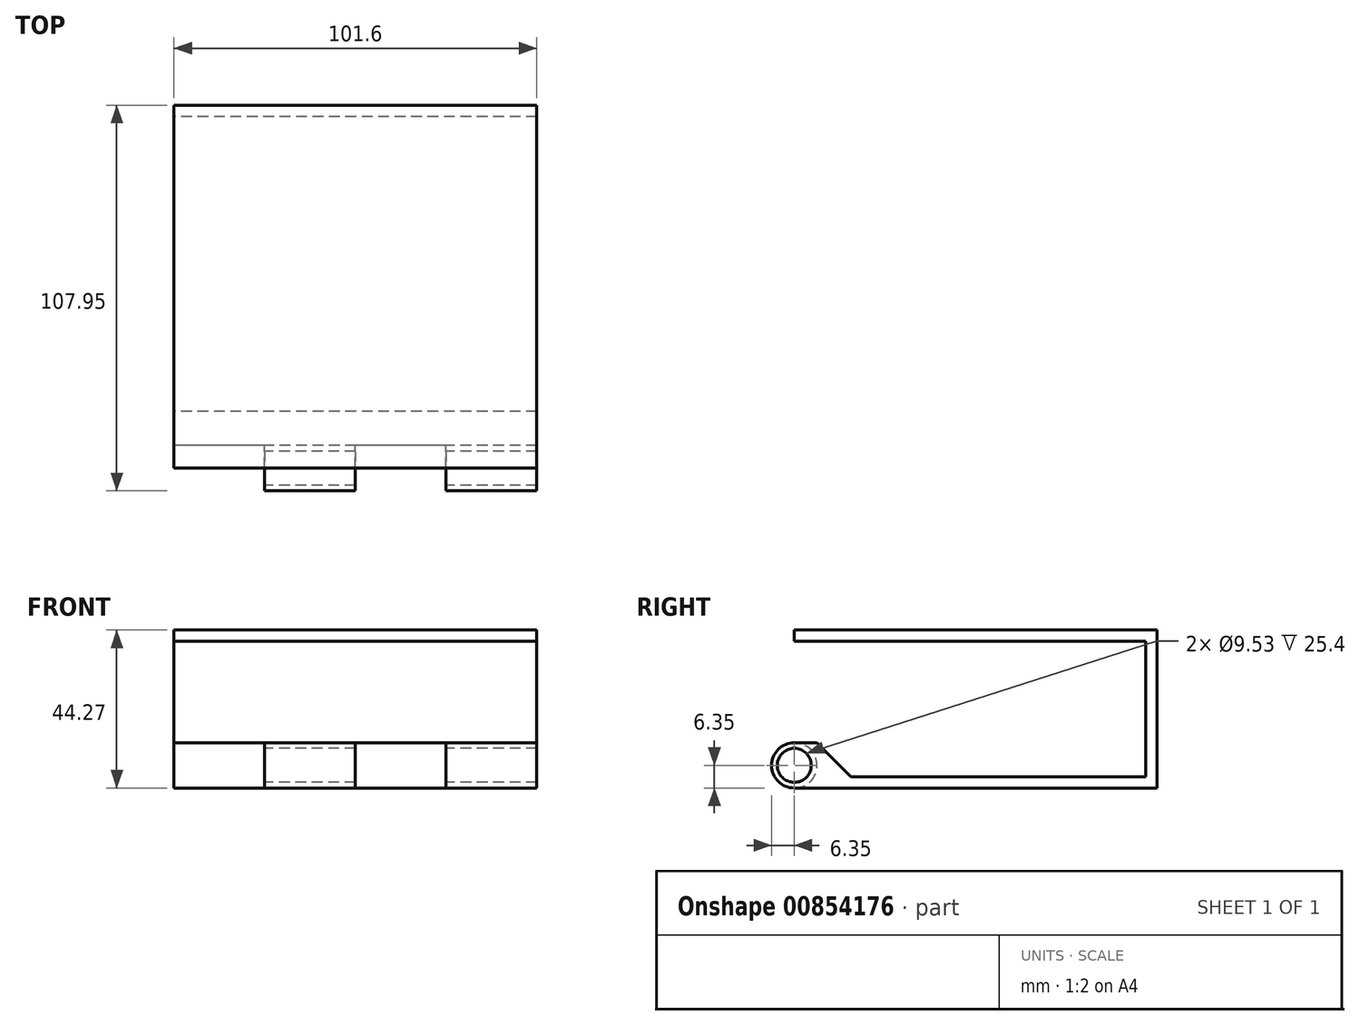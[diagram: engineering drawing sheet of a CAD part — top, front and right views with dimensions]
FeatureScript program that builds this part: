
annotation { "Feature Type Name" : "Feature", "Feature Type Description" : "" }
export const myFeature = defineFeature(function(context is Context, id is Id, definition is map)
    precondition{}
    {
        {
            var Q0;
            Q0=qCreatedBy(makeId("Right.planeOp"),FACE);
            var sketch = newSketch(context, id + "F0", { "sketchPlane" : qUnion([Q0])});
            skLineSegment(sketch, "E0.bottom", {"start": v(-44.45, 6.35) * mm, "end": v(-50.8, 6.35) * mm});
            skLineSegment(sketch, "E0.top", {"start": v(50.8, -6.35) * mm, "end": v(-50.8, -6.35) * mm});
            skLineSegment(sketch, "E0.left", {"start": v(50.8, 6.35) * mm, "end": v(50.8, -6.35) * mm});
            skLineSegment(sketch, "E0.right", {"start": v(-50.8, 6.35) * mm, "end": v(-50.8, -6.35) * mm});
            skPoint(sketch, "E0.middle", {"position": v(0, 0) * mm});
            skCircle(sketch, "E1", {"center": v(-50.8, 0) * mm, "radius": 6.35 * mm});
            skLineSegment(sketch, "E2", {"start": v(50.8, 6.35) * mm, "end": v(50.8, 37.92) * mm});
            skLineSegment(sketch, "E3", {"start": v(50.8, 37.92) * mm, "end": v(47.63, 37.92) * mm});
            skLineSegment(sketch, "E4", {"start": v(47.63, 34.74) * mm, "end": v(47.63, 6.35) * mm});
            skLineSegment(sketch, "E5.bottom", {"start": v(50.8, 37.92) * mm, "end": v(-50.8, 37.92) * mm});
            skLineSegment(sketch, "E5.top", {"start": v(47.62, 34.74) * mm, "end": v(-50.8, 34.74) * mm});
            skLineSegment(sketch, "E5.left", {"start": v(50.8, 34.74) * mm, "end": v(50.8, 37.92) * mm});
            skLineSegment(sketch, "E5.right", {"start": v(-50.8, 34.74) * mm, "end": v(-50.8, 37.92) * mm});
            skLineSegment(sketch, "E6", {"start": v(-44.45, 0) * mm, "end": v(-44.45, 6.35) * mm});
            skLineSegment(sketch, "E7", {"start": v(-44.45, 6.35) * mm, "end": v(-44.45, -6.35) * mm});
            skLineSegment(sketch, "E8", {"start": v(-44.45, 6.35) * mm, "end": v(-34.92, -3.18) * mm});
            skLineSegment(sketch, "E9", {"start": v(-34.92, -3.18) * mm, "end": v(47.63, -3.17) * mm});
            skLineSegment(sketch, "E10", {"start": v(47.62, -3.17) * mm, "end": v(47.62, 6.35) * mm});
            skCircle(sketch, "E11", {"center": v(-50.8, 0) * mm, "radius": 4.76 * mm});
            skSolve(sketch);
        }
        {
            var Q0;
            {var subQ7=sQuery(id+"F0.wireOp",EDGE,"E0.left");Q0=makeQuery(id+"F0.imprint","IMPRINT",FACE,{"disambiguationData":[TD([[makeQuery(id+"F0.imprint","IMPRINT",EDGE,{"derivedFrom":subQ7}),-1.0]])]});}
            var Q1;
            {var subQ1=sQuery(id+"F0.wireOp",EDGE,"E0.top");var subQ3=sQuery(id+"F0.wireOp",EDGE,"E7");var subQ4=makeQuery(id+"F0.imprint","INTERSECT",VERTEX,{"derivedFrom":[subQ1,subQ3]});Q1=makeQuery(id+"F0.imprint","IMPRINT",FACE,{"disambiguationData":[TD([[makeQuery(id+"F0.imprint","IMPRINT",EDGE,{"disambiguationData":[TD([[subQ4,1.0]])],"derivedFrom":subQ3}),-1.0]])]});}
            var Q2;
            {var subQ0=sQuery(id+"F0.wireOp",EDGE,"E0.bottom");Q2=makeQuery(id+"F0.imprint","IMPRINT",FACE,{"disambiguationData":[TD([[makeQuery(id+"F0.imprint","IMPRINT",EDGE,{"derivedFrom":subQ0}),1.0]])]});}
            extrude(context, id + "F1", {"entities" : qUnion([Q0, Q1, Q2]), "depth" : 101.6 * mm, "offsetDistance" : 25.4 * mm});
        }
        {
            var Q0;
            {var subQ0=sQuery(id+"F0.wireOp",EDGE,"E0.right");Q0=makeQuery(id+"F0.imprint","IMPRINT",FACE,{"disambiguationData":[TD([[makeQuery(id+"F0.imprint","IMPRINT",EDGE,{"derivedFrom":subQ0}),1.0]])]});}
            var Q1;
            {var subQ0=sQuery(id+"F0.wireOp",EDGE,"E0.right");Q1=makeQuery(id+"F0.imprint","IMPRINT",FACE,{"disambiguationData":[TD([[makeQuery(id+"F0.imprint","IMPRINT",EDGE,{"derivedFrom":subQ0}),-1.0]])]});}
            extrude(context, id + "F2", {"entities" : qUnion([Q0, Q1]), "operationType" : NewBodyOperationType.ADD, "depth" : 101.6 * mm, "offsetDistance" : 25.4 * mm});
        }
        {
            var Q0;
            {var subQ0=sQuery(id+"F0.wireOp",EDGE,"E0.right");Q0=makeQuery(id+"F0.imprint","IMPRINT",FACE,{"disambiguationData":[TD([[makeQuery(id+"F0.imprint","IMPRINT",EDGE,{"derivedFrom":subQ0}),-1.0]])]});}
            var Q1;
            {var subQ0=sQuery(id+"F0.wireOp",EDGE,"E0.right");Q1=makeQuery(id+"F0.imprint","IMPRINT",FACE,{"disambiguationData":[TD([[makeQuery(id+"F0.imprint","IMPRINT",EDGE,{"derivedFrom":subQ0}),1.0]])]});}
            extrude(context, id + "F3", {"entities" : qUnion([Q0, Q1]), "operationType" : NewBodyOperationType.REMOVE, "depth" : 76.2 * mm, "offsetDistance" : 25.4 * mm});
        }
        {
            var Q0;
            {var subQ0=sQuery(id+"F0.wireOp",EDGE,"E0.right");Q0=makeQuery(id+"F0.imprint","IMPRINT",FACE,{"disambiguationData":[TD([[makeQuery(id+"F0.imprint","IMPRINT",EDGE,{"derivedFrom":subQ0}),-1.0]])]});}
            var Q1;
            {var subQ0=sQuery(id+"F0.wireOp",EDGE,"E0.right");Q1=makeQuery(id+"F0.imprint","IMPRINT",FACE,{"disambiguationData":[TD([[makeQuery(id+"F0.imprint","IMPRINT",EDGE,{"derivedFrom":subQ0}),1.0]])]});}
            extrude(context, id + "F4", {"entities" : qUnion([Q0, Q1]), "operationType" : NewBodyOperationType.ADD, "depth" : 50.8 * mm, "offsetDistance" : 25.4 * mm});
        }
        {
            var Q0;
            {var subQ0=sQuery(id+"F0.wireOp",EDGE,"E0.right");Q0=makeQuery(id+"F0.imprint","IMPRINT",FACE,{"disambiguationData":[TD([[makeQuery(id+"F0.imprint","IMPRINT",EDGE,{"derivedFrom":subQ0}),1.0]])]});}
            var Q1;
            {var subQ0=sQuery(id+"F0.wireOp",EDGE,"E0.right");Q1=makeQuery(id+"F0.imprint","IMPRINT",FACE,{"disambiguationData":[TD([[makeQuery(id+"F0.imprint","IMPRINT",EDGE,{"derivedFrom":subQ0}),-1.0]])]});}
            extrude(context, id + "F5", {"entities" : qUnion([Q0, Q1]), "operationType" : NewBodyOperationType.REMOVE, "depth" : 25.4 * mm, "offsetDistance" : 25.4 * mm});
        }
    });
